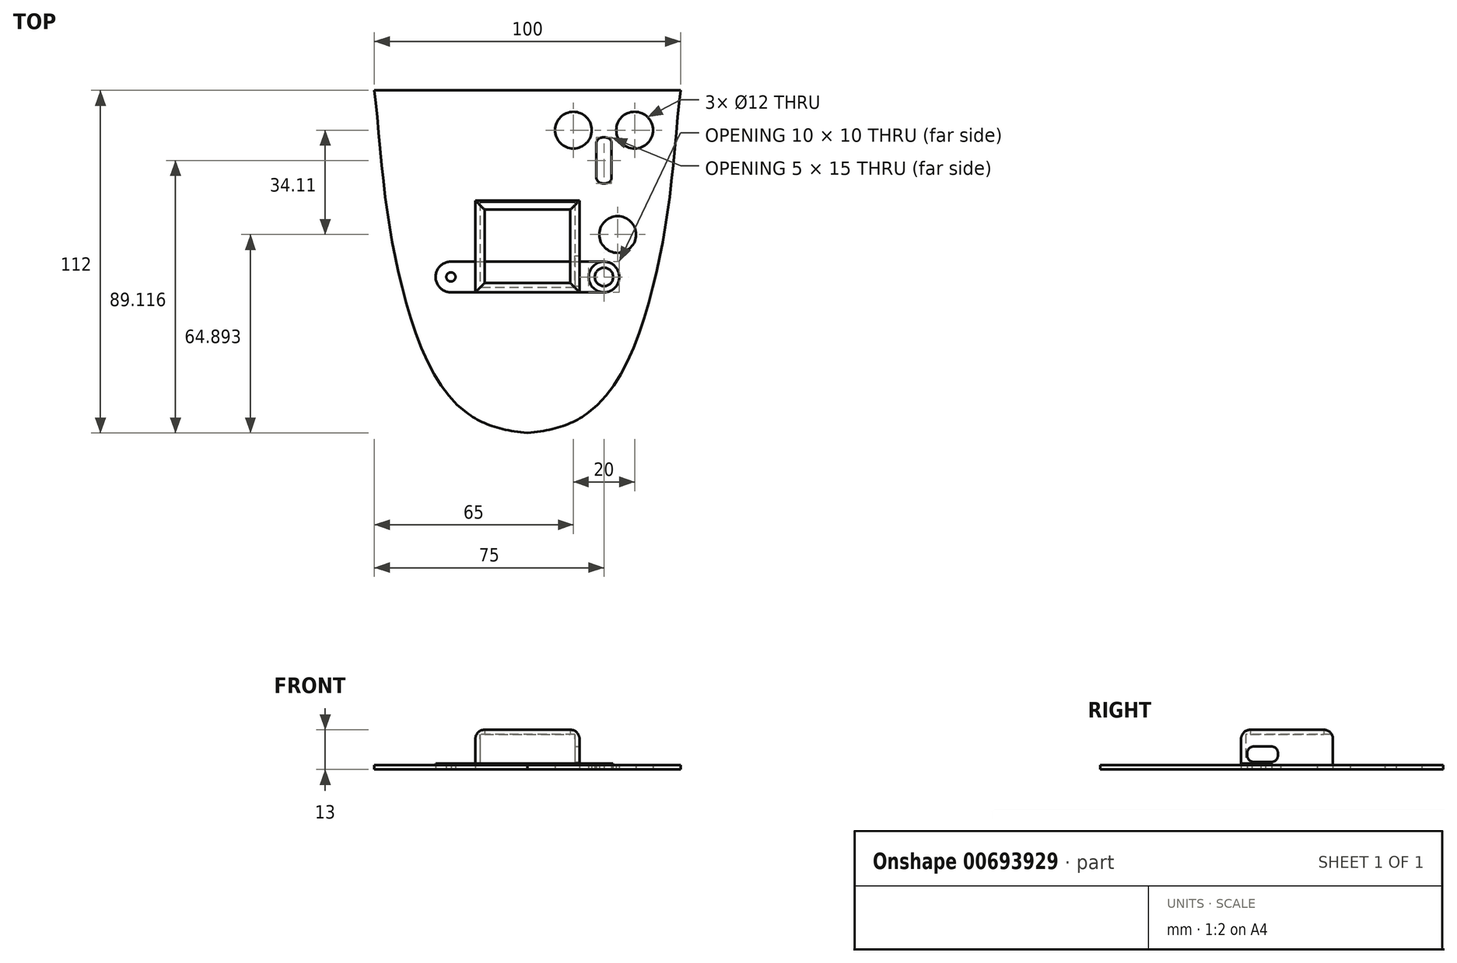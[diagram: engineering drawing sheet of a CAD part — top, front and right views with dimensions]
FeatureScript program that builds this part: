
annotation { "Feature Type Name" : "Feature", "Feature Type Description" : "" }
export const myFeature = defineFeature(function(context is Context, id is Id, definition is map)
    precondition{}
    {
        {
            var Q0;
            Q0=qCreatedBy(makeId("Top.planeOp"),FACE);
            var sketch = newSketch(context, id + "F0", { "sketchPlane" : qUnion([Q0])});
            skLineSegment(sketch, "E0", {"start": v(0, 74.67) * mm, "end": v(50, 74.67) * mm});
            skLineSegment(sketch, "E1", {"start": v(0, 74.67) * mm, "end": v(0, -37.33) * mm});
            skFitSpline(sketch, "E2", {"points": [v(50, 74.67) * mm, v(47, 44.67) * mm, v(42, 14.67) * mm, v(32, -15.33) * mm, v(19, -31.33) * mm, v(0, -37.33) * mm], "startDerivative": vector(-13.36, -107.56) * mm, "endDerivative": vector(-138.13, -13.22) * mm});
            skLineSegment(sketch, "E3.MirrorCS", {"start": v(0, 74.67) * mm, "end": v(-50, 74.67) * mm});
            skFitSpline(sketch, "E4.MirrorCS", {"points": [v(-50, 74.67) * mm, v(-47, 44.67) * mm, v(-42, 14.67) * mm, v(-32, -15.33) * mm, v(-19, -31.33) * mm, v(0, -37.33) * mm], "startDerivative": vector(13.36, -107.56) * mm, "endDerivative": vector(138.13, -13.22) * mm});
            skLineSegment(sketch, "E5.bottom", {"start": v(17, 38.67) * mm, "end": v(-17, 38.67) * mm});
            skLineSegment(sketch, "E5.top", {"start": v(17, 8.67) * mm, "end": v(-17, 8.67) * mm});
            skLineSegment(sketch, "E5.left", {"start": v(17, 38.67) * mm, "end": v(17, 8.67) * mm});
            skLineSegment(sketch, "E5.right", {"start": v(-17, 38.67) * mm, "end": v(-17, 8.67) * mm});
            skPoint(sketch, "E5.middle", {"position": v(0, 23.67) * mm});
            skCircle(sketch, "E6", {"center": v(-25, 13.67) * mm, "radius": 1.5 * mm});
            skCircle(sketch, "E7.MirrorC", {"center": v(25, 13.67) * mm, "radius": 1.5 * mm});
            skCircle(sketch, "E8", {"center": v(-25, 13.67) * mm, "radius": 3 * mm});
            skCircle(sketch, "E9.MirrorC", {"center": v(25, 13.67) * mm, "radius": 3 * mm});
            skLineSegment(sketch, "E10.left", {"start": v(0, 69.67) * mm, "end": v(0, 64.67) * mm});
            skLineSegment(sketch, "E11.bottom", {"start": v(20, 7.67) * mm, "end": v(-20, 7.67) * mm});
            skLineSegment(sketch, "E11.top", {"start": v(20, -58.33) * mm, "end": v(-20, -58.33) * mm});
            skLineSegment(sketch, "E11.left", {"start": v(20, 7.67) * mm, "end": v(20, -58.33) * mm});
            skLineSegment(sketch, "E11.right", {"start": v(-20, 7.67) * mm, "end": v(-20, -58.33) * mm});
            skPoint(sketch, "E11.middle", {"position": v(0, -25.33) * mm});
            skLineSegment(sketch, "E12.bottom", {"start": v(22.5, 59.29) * mm, "end": v(27.5, 59.29) * mm});
            skLineSegment(sketch, "E12.top", {"start": v(22.5, 44.29) * mm, "end": v(27.5, 44.29) * mm});
            skLineSegment(sketch, "E12.left", {"start": v(22.5, 59.29) * mm, "end": v(22.5, 44.29) * mm});
            skLineSegment(sketch, "E12.right", {"start": v(27.5, 59.29) * mm, "end": v(27.5, 44.29) * mm});
            skCircle(sketch, "E13", {"center": v(-25, 13.67) * mm, "radius": 5 * mm});
            skCircle(sketch, "E14.MirrorC", {"center": v(25, 13.67) * mm, "radius": 5 * mm});
            skLineSegment(sketch, "E15", {"start": v(-24.85, 18.67) * mm, "end": v(25, 18.67) * mm});
            skLineSegment(sketch, "E16", {"start": v(-25, 8.67) * mm, "end": v(25, 8.67) * mm});
            skLineSegment(sketch, "E17.bottom", {"start": v(14, 35.67) * mm, "end": v(-14, 35.67) * mm});
            skLineSegment(sketch, "E17.top", {"start": v(14, 11.67) * mm, "end": v(-14, 11.67) * mm});
            skLineSegment(sketch, "E17.left", {"start": v(14, 35.67) * mm, "end": v(14, 11.67) * mm});
            skLineSegment(sketch, "E17.right", {"start": v(-14, 35.67) * mm, "end": v(-14, 11.67) * mm});
            skCircle(sketch, "E18", {"center": v(-35, 61.67) * mm, "radius": 6 * mm});
            skCircle(sketch, "E19", {"center": v(-15, 61.67) * mm, "radius": 6 * mm});
            skCircle(sketch, "E20", {"center": v(-25, 47.67) * mm, "radius": 6 * mm});
            skCircle(sketch, "E21", {"center": v(-29.47, 27.56) * mm, "radius": 6 * mm});
            skCircle(sketch, "E22", {"center": v(-18.64, -7.33) * mm, "radius": 6 * mm});
            skCircle(sketch, "E23", {"center": v(0, -7.33) * mm, "radius": 6 * mm});
            skCircle(sketch, "E24", {"center": v(0, -27.12) * mm, "radius": 6 * mm});
            skCircle(sketch, "E25.MirrorC", {"center": v(35, 61.67) * mm, "radius": 6 * mm});
            skCircle(sketch, "E26.MirrorC", {"center": v(29.47, 27.56) * mm, "radius": 6 * mm});
            skCircle(sketch, "E27.MirrorC", {"center": v(18.64, -7.33) * mm, "radius": 6 * mm});
            skCircle(sketch, "E28.MirrorC", {"center": v(15, 61.67) * mm, "radius": 6 * mm});
            skSolve(sketch);
        }
        {
            var Q0;
            {var subQ6=sQuery(id+"F0.wireOp",EDGE,"E0");Q0=makeQuery(id+"F0.imprint","IMPRINT",FACE,{"disambiguationData":[TD([[makeQuery(id+"F0.imprint","IMPRINT",EDGE,{"derivedFrom":subQ6}),-1.0]])]});}
            var Q1;
            {var subQ1=sQuery(id+"F0.wireOp",EDGE,"E3.MirrorCS");Q1=makeQuery(id+"F0.imprint","IMPRINT",FACE,{"disambiguationData":[TD([[makeQuery(id+"F0.imprint","IMPRINT",EDGE,{"derivedFrom":subQ1}),1.0]])]});}
            var Q2;
            {var subQ5=sQuery(id+"F0.wireOp",EDGE,"E5.right");Q2=makeQuery(id+"F0.imprint","IMPRINT",FACE,{"disambiguationData":[TD([[makeQuery(id+"F0.imprint","IMPRINT",EDGE,{"derivedFrom":subQ5}),1.0]])]});}
            var Q3;
            {var subQ5=sQuery(id+"F0.wireOp",EDGE,"E5.left");Q3=makeQuery(id+"F0.imprint","IMPRINT",FACE,{"disambiguationData":[TD([[makeQuery(id+"F0.imprint","IMPRINT",EDGE,{"derivedFrom":subQ5}),-1.0]])]});}
            var Q4;
            Q4=makeQuery(id+"F0.imprint","IMPRINT",FACE,{"disambiguationData":[TD([[makeQuery(id+"F0.imprint","IMPRINT",EDGE,{"derivedFrom":sQuery(id+"F0.wireOp",EDGE,"E6")}),-1.0]])]});
            var Q5;
            Q5=makeQuery(id+"F0.imprint","IMPRINT",FACE,{"disambiguationData":[TD([[makeQuery(id+"F0.imprint","IMPRINT",EDGE,{"derivedFrom":sQuery(id+"F0.wireOp",EDGE,"E7.MirrorC")}),1.0]])]});
            var Q6;
            {var subQ0=sQuery(id+"F0.wireOp",EDGE,"E16");var subQ1=sQuery(id+"F0.wireOp",EDGE,"E5.right");var subQ2=makeQuery(id+"F0.imprint","INTERSECT",VERTEX,{"derivedFrom":[subQ1,subQ0]});Q6=makeQuery(id+"F0.imprint","IMPRINT",FACE,{"disambiguationData":[TD([[makeQuery(id+"F0.imprint","IMPRINT",EDGE,{"disambiguationData":[TD([[subQ2,1.0]])],"derivedFrom":subQ1}),-1.0]])]});}
            var Q7;
            Q7=makeQuery(id+"F0.imprint","IMPRINT",FACE,{"disambiguationData":[TD([[makeQuery(id+"F0.imprint","IMPRINT",EDGE,{"derivedFrom":sQuery(id+"F0.wireOp",EDGE,"E8")}),-1.0]])]});
            var Q8;
            {var subQ0=sQuery(id+"F0.wireOp",EDGE,"E16");var subQ1=sQuery(id+"F0.wireOp",EDGE,"E5.left");var subQ2=makeQuery(id+"F0.imprint","INTERSECT",VERTEX,{"derivedFrom":[subQ1,subQ0]});Q8=makeQuery(id+"F0.imprint","IMPRINT",FACE,{"disambiguationData":[TD([[makeQuery(id+"F0.imprint","IMPRINT",EDGE,{"disambiguationData":[TD([[subQ2,1.0]])],"derivedFrom":subQ1}),1.0]])]});}
            var Q9;
            Q9=makeQuery(id+"F0.imprint","IMPRINT",FACE,{"disambiguationData":[TD([[makeQuery(id+"F0.imprint","IMPRINT",EDGE,{"derivedFrom":sQuery(id+"F0.wireOp",EDGE,"E9.MirrorC")}),1.0]])]});
            var Q10;
            {var subQ3=sQuery(id+"F0.wireOp",EDGE,"E11.bottom");var subQ5=sQuery(id+"F0.wireOp",EDGE,"E11.right");var subQ7=makeQuery(id+"F0.imprint","INTERSECT",VERTEX,{"derivedFrom":[subQ3,subQ5]});Q10=makeQuery(id+"F0.imprint","IMPRINT",FACE,{"disambiguationData":[TD([[makeQuery(id+"F0.imprint","IMPRINT",EDGE,{"disambiguationData":[TD([[subQ7,1.0]])],"derivedFrom":subQ3}),1.0]])]});}
            var Q11;
            {var subQ3=sQuery(id+"F0.wireOp",EDGE,"E11.bottom");var subQ5=sQuery(id+"F0.wireOp",EDGE,"E11.left");var subQ6=makeQuery(id+"F0.imprint","INTERSECT",VERTEX,{"derivedFrom":[subQ3,subQ5]});Q11=makeQuery(id+"F0.imprint","IMPRINT",FACE,{"disambiguationData":[TD([[makeQuery(id+"F0.imprint","IMPRINT",EDGE,{"disambiguationData":[TD([[subQ6,-1.0]])],"derivedFrom":subQ3}),1.0]])]});}
            var Q12;
            {var subQ0=sQuery(id+"F0.wireOp",EDGE,"E17.bottom");var subQ1=sQuery(id+"F0.wireOp",EDGE,"E1");var subQ2=makeQuery(id+"F0.imprint","INTERSECT",VERTEX,{"derivedFrom":[subQ1,subQ0]});Q12=makeQuery(id+"F0.imprint","IMPRINT",FACE,{"disambiguationData":[TD([[makeQuery(id+"F0.imprint","IMPRINT",EDGE,{"disambiguationData":[TD([[subQ2,-1.0]])],"derivedFrom":subQ1}),-1.0]])]});}
            var Q13;
            {var subQ0=sQuery(id+"F0.wireOp",EDGE,"E17.bottom");var subQ1=sQuery(id+"F0.wireOp",EDGE,"E1");var subQ2=makeQuery(id+"F0.imprint","INTERSECT",VERTEX,{"derivedFrom":[subQ1,subQ0]});Q13=makeQuery(id+"F0.imprint","IMPRINT",FACE,{"disambiguationData":[TD([[makeQuery(id+"F0.imprint","IMPRINT",EDGE,{"disambiguationData":[TD([[subQ2,-1.0]])],"derivedFrom":subQ1}),1.0]])]});}
            var Q14;
            {var subQ0=sQuery(id+"F0.wireOp",EDGE,"E15");var subQ1=sQuery(id+"F0.wireOp",EDGE,"E1");var subQ2=makeQuery(id+"F0.imprint","INTERSECT",VERTEX,{"derivedFrom":[subQ1,subQ0]});Q14=makeQuery(id+"F0.imprint","IMPRINT",FACE,{"disambiguationData":[TD([[makeQuery(id+"F0.imprint","IMPRINT",EDGE,{"disambiguationData":[TD([[subQ2,-1.0]])],"derivedFrom":subQ1}),1.0]])]});}
            var Q15;
            {var subQ0=sQuery(id+"F0.wireOp",EDGE,"E15");var subQ1=sQuery(id+"F0.wireOp",EDGE,"E1");var subQ2=makeQuery(id+"F0.imprint","INTERSECT",VERTEX,{"derivedFrom":[subQ1,subQ0]});Q15=makeQuery(id+"F0.imprint","IMPRINT",FACE,{"disambiguationData":[TD([[makeQuery(id+"F0.imprint","IMPRINT",EDGE,{"disambiguationData":[TD([[subQ2,-1.0]])],"derivedFrom":subQ1}),-1.0]])]});}
            var Q16;
            Q16=makeQuery(id+"F0.imprint","IMPRINT",FACE,{"disambiguationData":[TD([[makeQuery(id+"F0.imprint","IMPRINT",EDGE,{"derivedFrom":sQuery(id+"F0.wireOp",EDGE,"E18")}),1.0]])]});
            var Q17;
            Q17=makeQuery(id+"F0.imprint","IMPRINT",FACE,{"disambiguationData":[TD([[makeQuery(id+"F0.imprint","IMPRINT",EDGE,{"derivedFrom":sQuery(id+"F0.wireOp",EDGE,"E19")}),1.0]])]});
            var Q18;
            Q18=makeQuery(id+"F0.imprint","IMPRINT",FACE,{"disambiguationData":[TD([[makeQuery(id+"F0.imprint","IMPRINT",EDGE,{"derivedFrom":sQuery(id+"F0.wireOp",EDGE,"E20")}),1.0]])]});
            var Q19;
            Q19=makeQuery(id+"F0.imprint","IMPRINT",FACE,{"disambiguationData":[TD([[makeQuery(id+"F0.imprint","IMPRINT",EDGE,{"derivedFrom":sQuery(id+"F0.wireOp",EDGE,"E21")}),1.0]])]});
            var Q20;
            Q20=makeQuery(id+"F0.imprint","IMPRINT",FACE,{"disambiguationData":[TD([[makeQuery(id+"F0.imprint","IMPRINT",EDGE,{"derivedFrom":sQuery(id+"F0.wireOp",EDGE,"E28.MirrorC")}),-1.0]])]});
            var Q21;
            Q21=makeQuery(id+"F0.imprint","IMPRINT",FACE,{"disambiguationData":[TD([[makeQuery(id+"F0.imprint","IMPRINT",EDGE,{"derivedFrom":sQuery(id+"F0.wireOp",EDGE,"E25.MirrorC")}),-1.0]])]});
            var Q22;
            Q22=makeQuery(id+"F0.imprint","IMPRINT",FACE,{"disambiguationData":[TD([[makeQuery(id+"F0.imprint","IMPRINT",EDGE,{"derivedFrom":sQuery(id+"F0.wireOp",EDGE,"E26.MirrorC")}),-1.0]])]});
            var Q23;
            {var subQ0=sQuery(id+"F0.wireOp",EDGE,"E27.MirrorC");var subQ1=sQuery(id+"F0.wireOp",EDGE,"E11.left");var subQ2=makeQuery(id+"F0.imprint","INTERSECT",VERTEX,{"disambiguationData":[OD(0.0)],"derivedFrom":[subQ1,subQ0]});Q23=makeQuery(id+"F0.imprint","IMPRINT",FACE,{"disambiguationData":[TD([[makeQuery(id+"F0.imprint","IMPRINT",EDGE,{"disambiguationData":[TD([[subQ2,-1.0]])],"derivedFrom":subQ1}),1.0]])]});}
            var Q24;
            {var subQ0=sQuery(id+"F0.wireOp",EDGE,"E27.MirrorC");var subQ1=sQuery(id+"F0.wireOp",EDGE,"E11.left");var subQ2=makeQuery(id+"F0.imprint","INTERSECT",VERTEX,{"disambiguationData":[OD(0.0)],"derivedFrom":[subQ1,subQ0]});Q24=makeQuery(id+"F0.imprint","IMPRINT",FACE,{"disambiguationData":[TD([[makeQuery(id+"F0.imprint","IMPRINT",EDGE,{"disambiguationData":[TD([[subQ2,-1.0]])],"derivedFrom":subQ1}),-1.0]])]});}
            var Q25;
            {var subQ0=sQuery(id+"F0.wireOp",EDGE,"E23");var subQ1=sQuery(id+"F0.wireOp",EDGE,"E1");var subQ2=makeQuery(id+"F0.imprint","INTERSECT",VERTEX,{"disambiguationData":[OD(0.0)],"derivedFrom":[subQ1,subQ0]});Q25=makeQuery(id+"F0.imprint","IMPRINT",FACE,{"disambiguationData":[TD([[makeQuery(id+"F0.imprint","IMPRINT",EDGE,{"disambiguationData":[TD([[subQ2,-1.0]])],"derivedFrom":subQ1}),1.0]])]});}
            var Q26;
            {var subQ0=sQuery(id+"F0.wireOp",EDGE,"E23");var subQ1=sQuery(id+"F0.wireOp",EDGE,"E1");var subQ2=makeQuery(id+"F0.imprint","INTERSECT",VERTEX,{"disambiguationData":[OD(0.0)],"derivedFrom":[subQ1,subQ0]});Q26=makeQuery(id+"F0.imprint","IMPRINT",FACE,{"disambiguationData":[TD([[makeQuery(id+"F0.imprint","IMPRINT",EDGE,{"disambiguationData":[TD([[subQ2,-1.0]])],"derivedFrom":subQ1}),-1.0]])]});}
            var Q27;
            {var subQ0=sQuery(id+"F0.wireOp",EDGE,"E22");var subQ1=sQuery(id+"F0.wireOp",EDGE,"E11.right");var subQ2=makeQuery(id+"F0.imprint","INTERSECT",VERTEX,{"disambiguationData":[OD(0.0)],"derivedFrom":[subQ1,subQ0]});Q27=makeQuery(id+"F0.imprint","IMPRINT",FACE,{"disambiguationData":[TD([[makeQuery(id+"F0.imprint","IMPRINT",EDGE,{"disambiguationData":[TD([[subQ2,-1.0]])],"derivedFrom":subQ1}),1.0]])]});}
            var Q28;
            {var subQ0=sQuery(id+"F0.wireOp",EDGE,"E22");var subQ1=sQuery(id+"F0.wireOp",EDGE,"E11.right");var subQ2=makeQuery(id+"F0.imprint","INTERSECT",VERTEX,{"disambiguationData":[OD(0.0)],"derivedFrom":[subQ1,subQ0]});Q28=makeQuery(id+"F0.imprint","IMPRINT",FACE,{"disambiguationData":[TD([[makeQuery(id+"F0.imprint","IMPRINT",EDGE,{"disambiguationData":[TD([[subQ2,-1.0]])],"derivedFrom":subQ1}),-1.0]])]});}
            var Q29;
            {var subQ0=sQuery(id+"F0.wireOp",EDGE,"E24");var subQ1=sQuery(id+"F0.wireOp",EDGE,"E1");var subQ2=makeQuery(id+"F0.imprint","INTERSECT",VERTEX,{"disambiguationData":[OD(0.0)],"derivedFrom":[subQ1,subQ0]});Q29=makeQuery(id+"F0.imprint","IMPRINT",FACE,{"disambiguationData":[TD([[makeQuery(id+"F0.imprint","IMPRINT",EDGE,{"disambiguationData":[TD([[subQ2,-1.0]])],"derivedFrom":subQ1}),-1.0]])]});}
            var Q30;
            {var subQ0=sQuery(id+"F0.wireOp",EDGE,"E24");var subQ1=sQuery(id+"F0.wireOp",EDGE,"E1");var subQ2=makeQuery(id+"F0.imprint","INTERSECT",VERTEX,{"disambiguationData":[OD(0.0)],"derivedFrom":[subQ1,subQ0]});Q30=makeQuery(id+"F0.imprint","IMPRINT",FACE,{"disambiguationData":[TD([[makeQuery(id+"F0.imprint","IMPRINT",EDGE,{"disambiguationData":[TD([[subQ2,-1.0]])],"derivedFrom":subQ1}),1.0]])]});}
            extrude(context, id + "F1", {"entities" : qUnion([Q0, Q1, Q2, Q3, Q4, Q5, Q6, Q7, Q8, Q9, Q10, Q11, Q12, Q13, Q14, Q15, Q16, Q17, Q18, Q19, Q20, Q21, Q22, Q23, Q24, Q25, Q26, Q27, Q28, Q29, Q30]), "depth" : 1.5 * mm, "offsetDistance" : 25 * mm});
        }
        {
            var Q0;
            {var subQ0=sQuery(id+"F0.wireOp",EDGE,"E17.bottom");var subQ1=sQuery(id+"F0.wireOp",EDGE,"E1");var subQ2=makeQuery(id+"F0.imprint","INTERSECT",VERTEX,{"derivedFrom":[subQ1,subQ0]});Q0=makeQuery(id+"F0.imprint","IMPRINT",FACE,{"disambiguationData":[TD([[makeQuery(id+"F0.imprint","IMPRINT",EDGE,{"disambiguationData":[TD([[subQ2,-1.0]])],"derivedFrom":subQ1}),-1.0]])]});}
            var Q1;
            {var subQ0=sQuery(id+"F0.wireOp",EDGE,"E17.bottom");var subQ1=sQuery(id+"F0.wireOp",EDGE,"E1");var subQ2=makeQuery(id+"F0.imprint","INTERSECT",VERTEX,{"derivedFrom":[subQ1,subQ0]});Q1=makeQuery(id+"F0.imprint","IMPRINT",FACE,{"disambiguationData":[TD([[makeQuery(id+"F0.imprint","IMPRINT",EDGE,{"disambiguationData":[TD([[subQ2,-1.0]])],"derivedFrom":subQ1}),1.0]])]});}
            var Q2;
            {var subQ0=sQuery(id+"F0.wireOp",EDGE,"E15");var subQ1=sQuery(id+"F0.wireOp",EDGE,"E1");var subQ2=makeQuery(id+"F0.imprint","INTERSECT",VERTEX,{"derivedFrom":[subQ1,subQ0]});Q2=makeQuery(id+"F0.imprint","IMPRINT",FACE,{"disambiguationData":[TD([[makeQuery(id+"F0.imprint","IMPRINT",EDGE,{"disambiguationData":[TD([[subQ2,-1.0]])],"derivedFrom":subQ1}),1.0]])]});}
            var Q3;
            {var subQ0=sQuery(id+"F0.wireOp",EDGE,"E15");var subQ1=sQuery(id+"F0.wireOp",EDGE,"E1");var subQ2=makeQuery(id+"F0.imprint","INTERSECT",VERTEX,{"derivedFrom":[subQ1,subQ0]});Q3=makeQuery(id+"F0.imprint","IMPRINT",FACE,{"disambiguationData":[TD([[makeQuery(id+"F0.imprint","IMPRINT",EDGE,{"disambiguationData":[TD([[subQ2,-1.0]])],"derivedFrom":subQ1}),-1.0]])]});}
            var Q4;
            {var subQ5=sQuery(id+"F0.wireOp",EDGE,"E5.bottom");var subQ7=sQuery(id+"F0.wireOp",EDGE,"E1");var subQ8=makeQuery(id+"F0.imprint","INTERSECT",VERTEX,{"derivedFrom":[subQ7,subQ5]});Q4=makeQuery(id+"F0.imprint","IMPRINT",FACE,{"disambiguationData":[TD([[makeQuery(id+"F0.imprint","IMPRINT",EDGE,{"disambiguationData":[TD([[subQ8,-1.0]])],"derivedFrom":subQ7}),-1.0]])]});}
            var Q5;
            {var subQ1=sQuery(id+"F0.wireOp",EDGE,"E5.bottom");var subQ7=sQuery(id+"F0.wireOp",EDGE,"E1");var subQ8=makeQuery(id+"F0.imprint","INTERSECT",VERTEX,{"derivedFrom":[subQ7,subQ1]});Q5=makeQuery(id+"F0.imprint","IMPRINT",FACE,{"disambiguationData":[TD([[makeQuery(id+"F0.imprint","IMPRINT",EDGE,{"disambiguationData":[TD([[subQ8,-1.0]])],"derivedFrom":subQ7}),1.0]])]});}
            var Q6;
            {var subQ3=sQuery(id+"F0.wireOp",EDGE,"E1");var subQ9=sQuery(id+"F0.wireOp",EDGE,"E17.top");var subQ11=makeQuery(id+"F0.imprint","INTERSECT",VERTEX,{"derivedFrom":[subQ3,subQ9]});Q6=makeQuery(id+"F0.imprint","IMPRINT",FACE,{"disambiguationData":[TD([[makeQuery(id+"F0.imprint","IMPRINT",EDGE,{"disambiguationData":[TD([[subQ11,-1.0]])],"derivedFrom":subQ3}),1.0]])]});}
            var Q7;
            {var subQ3=sQuery(id+"F0.wireOp",EDGE,"E1");var subQ9=sQuery(id+"F0.wireOp",EDGE,"E17.top");var subQ10=makeQuery(id+"F0.imprint","INTERSECT",VERTEX,{"derivedFrom":[subQ3,subQ9]});Q7=makeQuery(id+"F0.imprint","IMPRINT",FACE,{"disambiguationData":[TD([[makeQuery(id+"F0.imprint","IMPRINT",EDGE,{"disambiguationData":[TD([[subQ10,-1.0]])],"derivedFrom":subQ3}),-1.0]])]});}
            extrude(context, id + "F2", {"entities" : qUnion([Q0, Q1, Q2, Q3, Q4, Q5, Q6, Q7]), "depth" : 13 * mm, "offsetDistance" : 25 * mm});
        }
        {
            var Q0;
            Q0=makeQuery(id+"F2.opExtrude","SWEPT_FACE",FACE,{"disambiguationData":[OSD([sQuery(id+"F0.wireOp",EDGE,"E16")])]});
            var Q1;
            Q1=makeQuery(id+"F2.opExtrude","SWEPT_FACE",FACE,{"disambiguationData":[OSD([sQuery(id+"F0.wireOp",EDGE,"E5.bottom")])]});
            shell(context, id + "F3", {"entities" : qUnion([Q0, Q1]), "thickness" : 1.5 * mm});
        }
        {
            var Q0;
            Q0=makeQuery(id+"F2.opExtrude","CAP_EDGE",EDGE,{"disambiguationData":[OSD([sQuery(id+"F0.wireOp",EDGE,"E5.right")])],"isStart":false});
            var Q1;
            Q1=makeQuery(id+"F2.opExtrude","CAP_EDGE",EDGE,{"disambiguationData":[OSD([sQuery(id+"F0.wireOp",EDGE,"E5.left")])],"isStart":false});
            var Q2;
            Q2=makeQuery(id+"F2.opExtrude","CAP_EDGE",EDGE,{"disambiguationData":[OSD([sQuery(id+"F0.wireOp",EDGE,"E5.top")])],"isStart":false});
            var Q3;
            Q3=makeQuery(id+"F2.opExtrude","CAP_EDGE",EDGE,{"disambiguationData":[OSD([sQuery(id+"F0.wireOp",EDGE,"E5.bottom")])],"isStart":false});
            var Q4;
            Q4=makeQuery(id+"F2.opExtrude","CAP_EDGE",EDGE,{"disambiguationData":[OSD([sQuery(id+"F0.wireOp",EDGE,"E16")])],"isStart":false});
            fillet(context, id + "F4", {"entities" : qUnion([Q0, Q1, Q2, Q3, Q4]), "radius" : 3 * mm, "tangentPropagation" : true, "allowEdgeOverflow" : false});
        }
        {
            var Q0;
            Q0=makeQuery(id+"F1.opExtrude","SWEPT_EDGE",EDGE,{"disambiguationData":[OSD([sQuery(id+"F0.wireOp",EDGE,"E12.bottom"),sQuery(id+"F0.wireOp",EDGE,"E12.left")])]});
            var Q1;
            Q1=makeQuery(id+"F1.opExtrude","SWEPT_EDGE",EDGE,{"disambiguationData":[OSD([sQuery(id+"F0.wireOp",EDGE,"E12.bottom"),sQuery(id+"F0.wireOp",EDGE,"E12.right")])]});
            var Q2;
            Q2=makeQuery(id+"F1.opExtrude","SWEPT_EDGE",EDGE,{"disambiguationData":[OSD([sQuery(id+"F0.wireOp",EDGE,"E12.top"),sQuery(id+"F0.wireOp",EDGE,"E12.right")])]});
            var Q3;
            Q3=makeQuery(id+"F1.opExtrude","SWEPT_EDGE",EDGE,{"disambiguationData":[OSD([sQuery(id+"F0.wireOp",EDGE,"E12.top"),sQuery(id+"F0.wireOp",EDGE,"E12.left")])]});
            fillet(context, id + "F5", {"entities" : qUnion([Q0, Q1, Q2, Q3]), "radius" : 2 * mm, "tangentPropagation" : true, "allowEdgeOverflow" : false});
        }
        {
            var Q0;
            {var subQ0=sQuery(id+"F0.wireOp",EDGE,"E15");var subQ1=sQuery(id+"F0.wireOp",EDGE,"E1");var subQ2=makeQuery(id+"F0.imprint","INTERSECT",VERTEX,{"derivedFrom":[subQ1,subQ0]});Q0=makeQuery(id+"F0.imprint","IMPRINT",FACE,{"disambiguationData":[TD([[makeQuery(id+"F0.imprint","IMPRINT",EDGE,{"disambiguationData":[TD([[subQ2,-1.0]])],"derivedFrom":subQ1}),-1.0]])]});}
            var Q1;
            {var subQ0=sQuery(id+"F0.wireOp",EDGE,"E15");var subQ1=sQuery(id+"F0.wireOp",EDGE,"E1");var subQ2=makeQuery(id+"F0.imprint","INTERSECT",VERTEX,{"derivedFrom":[subQ1,subQ0]});Q1=makeQuery(id+"F0.imprint","IMPRINT",FACE,{"disambiguationData":[TD([[makeQuery(id+"F0.imprint","IMPRINT",EDGE,{"disambiguationData":[TD([[subQ2,-1.0]])],"derivedFrom":subQ1}),1.0]])]});}
            var Q2;
            {var subQ0=sQuery(id+"F0.wireOp",EDGE,"E16");var subQ1=sQuery(id+"F0.wireOp",EDGE,"E5.left");var subQ2=makeQuery(id+"F0.imprint","INTERSECT",VERTEX,{"derivedFrom":[subQ1,subQ0]});Q2=makeQuery(id+"F0.imprint","IMPRINT",FACE,{"disambiguationData":[TD([[makeQuery(id+"F0.imprint","IMPRINT",EDGE,{"disambiguationData":[TD([[subQ2,1.0]])],"derivedFrom":subQ1}),1.0]])]});}
            var Q3;
            Q3=makeQuery(id+"F0.imprint","IMPRINT",FACE,{"disambiguationData":[TD([[makeQuery(id+"F0.imprint","IMPRINT",EDGE,{"derivedFrom":sQuery(id+"F0.wireOp",EDGE,"E9.MirrorC")}),1.0]])]});
            var Q4;
            Q4=makeQuery(id+"F0.imprint","IMPRINT",FACE,{"disambiguationData":[TD([[makeQuery(id+"F0.imprint","IMPRINT",EDGE,{"derivedFrom":sQuery(id+"F0.wireOp",EDGE,"E7.MirrorC")}),1.0]])]});
            var Q5;
            Q5=makeQuery(id+"F0.imprint","IMPRINT",FACE,{"disambiguationData":[TD([[makeQuery(id+"F0.imprint","IMPRINT",EDGE,{"derivedFrom":sQuery(id+"F0.wireOp",EDGE,"E8")}),-1.0]])]});
            var Q6;
            Q6=makeQuery(id+"F0.imprint","IMPRINT",FACE,{"disambiguationData":[TD([[makeQuery(id+"F0.imprint","IMPRINT",EDGE,{"derivedFrom":sQuery(id+"F0.wireOp",EDGE,"E6")}),-1.0]])]});
            var Q7;
            {var subQ0=sQuery(id+"F0.wireOp",EDGE,"E16");var subQ1=sQuery(id+"F0.wireOp",EDGE,"E5.right");var subQ2=makeQuery(id+"F0.imprint","INTERSECT",VERTEX,{"derivedFrom":[subQ1,subQ0]});Q7=makeQuery(id+"F0.imprint","IMPRINT",FACE,{"disambiguationData":[TD([[makeQuery(id+"F0.imprint","IMPRINT",EDGE,{"disambiguationData":[TD([[subQ2,1.0]])],"derivedFrom":subQ1}),-1.0]])]});}
            var Q8;
            {var subQ3=sQuery(id+"F0.wireOp",EDGE,"E1");var subQ9=sQuery(id+"F0.wireOp",EDGE,"E17.top");var subQ10=makeQuery(id+"F0.imprint","INTERSECT",VERTEX,{"derivedFrom":[subQ3,subQ9]});Q8=makeQuery(id+"F0.imprint","IMPRINT",FACE,{"disambiguationData":[TD([[makeQuery(id+"F0.imprint","IMPRINT",EDGE,{"disambiguationData":[TD([[subQ10,-1.0]])],"derivedFrom":subQ3}),-1.0]])]});}
            var Q9;
            {var subQ3=sQuery(id+"F0.wireOp",EDGE,"E1");var subQ9=sQuery(id+"F0.wireOp",EDGE,"E17.top");var subQ11=makeQuery(id+"F0.imprint","INTERSECT",VERTEX,{"derivedFrom":[subQ3,subQ9]});Q9=makeQuery(id+"F0.imprint","IMPRINT",FACE,{"disambiguationData":[TD([[makeQuery(id+"F0.imprint","IMPRINT",EDGE,{"disambiguationData":[TD([[subQ11,-1.0]])],"derivedFrom":subQ3}),1.0]])]});}
            extrude(context, id + "F6", {"entities" : qUnion([Q0, Q1, Q2, Q3, Q4, Q5, Q6, Q7, Q8, Q9]), "depth" : 2 * mm, "offsetDistance" : 25 * mm});
        }
        {
            var Q0;
            {var subQ0=sQuery(id+"F0.wireOp",EDGE,"E17.bottom");var subQ1=sQuery(id+"F0.wireOp",EDGE,"E1");var subQ2=makeQuery(id+"F0.imprint","INTERSECT",VERTEX,{"derivedFrom":[subQ1,subQ0]});Q0=makeQuery(id+"F0.imprint","IMPRINT",FACE,{"disambiguationData":[TD([[makeQuery(id+"F0.imprint","IMPRINT",EDGE,{"disambiguationData":[TD([[subQ2,-1.0]])],"derivedFrom":subQ1}),-1.0]])]});}
            var Q1;
            {var subQ0=sQuery(id+"F0.wireOp",EDGE,"E17.bottom");var subQ1=sQuery(id+"F0.wireOp",EDGE,"E1");var subQ2=makeQuery(id+"F0.imprint","INTERSECT",VERTEX,{"derivedFrom":[subQ1,subQ0]});Q1=makeQuery(id+"F0.imprint","IMPRINT",FACE,{"disambiguationData":[TD([[makeQuery(id+"F0.imprint","IMPRINT",EDGE,{"disambiguationData":[TD([[subQ2,-1.0]])],"derivedFrom":subQ1}),1.0]])]});}
            var Q2;
            {var subQ0=sQuery(id+"F0.wireOp",EDGE,"E15");var subQ1=sQuery(id+"F0.wireOp",EDGE,"E1");var subQ2=makeQuery(id+"F0.imprint","INTERSECT",VERTEX,{"derivedFrom":[subQ1,subQ0]});Q2=makeQuery(id+"F0.imprint","IMPRINT",FACE,{"disambiguationData":[TD([[makeQuery(id+"F0.imprint","IMPRINT",EDGE,{"disambiguationData":[TD([[subQ2,-1.0]])],"derivedFrom":subQ1}),1.0]])]});}
            var Q3;
            {var subQ0=sQuery(id+"F0.wireOp",EDGE,"E15");var subQ1=sQuery(id+"F0.wireOp",EDGE,"E1");var subQ2=makeQuery(id+"F0.imprint","INTERSECT",VERTEX,{"derivedFrom":[subQ1,subQ0]});Q3=makeQuery(id+"F0.imprint","IMPRINT",FACE,{"disambiguationData":[TD([[makeQuery(id+"F0.imprint","IMPRINT",EDGE,{"disambiguationData":[TD([[subQ2,-1.0]])],"derivedFrom":subQ1}),-1.0]])]});}
            extrude(context, id + "F7", {"entities" : qUnion([Q0, Q1, Q2, Q3]), "operationType" : NewBodyOperationType.REMOVE, "depth" : 25 * mm, "offsetDistance" : 25 * mm, "hasSecondDirection" : true, "secondDirectionOppositeDirection" : false, "secondDirectionDepth" : 3 * mm});
        }
        {
            var Q0;
            Q0=makeQuery(id+"F2.opExtrude","SWEPT_FACE",FACE,{"disambiguationData":[OSD([sQuery(id+"F0.wireOp",EDGE,"E5.left")])]});
            var sketch = newSketch(context, id + "F8", { "sketchPlane" : qUnion([Q0])});
            skLineSegment(sketch, "E29.bottom", {"start": v(10.67, 7.5) * mm, "end": v(20.67, 7.5) * mm});
            skLineSegment(sketch, "E29.top", {"start": v(10.67, 2.5) * mm, "end": v(20.67, 2.5) * mm});
            skLineSegment(sketch, "E29.left", {"start": v(10.67, 7.5) * mm, "end": v(10.67, 2.5) * mm});
            skLineSegment(sketch, "E29.right", {"start": v(20.67, 7.5) * mm, "end": v(20.67, 2.5) * mm});
            skSolve(sketch);
        }
        {
            var Q0;
            Q0=makeQuery(id+"F8.imprint","IMPRINT",FACE,{"disambiguationData":[TD([[makeQuery(id+"F8.imprint","IMPRINT",EDGE,{"derivedFrom":sQuery(id+"F8.wireOp",EDGE,"E29.bottom")}),-1.0]])]});
            extrude(context, id + "F9", {"entities" : qUnion([Q0]), "operationType" : NewBodyOperationType.REMOVE, "oppositeDirection" : true, "depth" : 5 * mm, "offsetDistance" : 25 * mm});
        }
        {
            var Q0;
            Q0=makeQuery(id+"F9.boolean.opBoolean","COPY",EDGE,{"derivedFrom":makeQuery(id+"F9.opExtrude","SWEPT_EDGE",EDGE,{"disambiguationData":[OSD([sQuery(id+"F8.wireOp",EDGE,"E29.top"),sQuery(id+"F8.wireOp",EDGE,"E29.right")])]})});
            var Q1;
            Q1=makeQuery(id+"F9.boolean.opBoolean","COPY",EDGE,{"derivedFrom":makeQuery(id+"F9.opExtrude","SWEPT_EDGE",EDGE,{"disambiguationData":[OSD([sQuery(id+"F8.wireOp",EDGE,"E29.bottom"),sQuery(id+"F8.wireOp",EDGE,"E29.right")])]})});
            var Q2;
            Q2=makeQuery(id+"F9.boolean.opBoolean","COPY",EDGE,{"derivedFrom":makeQuery(id+"F9.opExtrude","SWEPT_EDGE",EDGE,{"disambiguationData":[OSD([sQuery(id+"F8.wireOp",EDGE,"E29.bottom"),sQuery(id+"F8.wireOp",EDGE,"E29.left")])]})});
            var Q3;
            Q3=makeQuery(id+"F9.boolean.opBoolean","COPY",EDGE,{"derivedFrom":makeQuery(id+"F9.opExtrude","SWEPT_EDGE",EDGE,{"disambiguationData":[OSD([sQuery(id+"F8.wireOp",EDGE,"E29.top"),sQuery(id+"F8.wireOp",EDGE,"E29.left")])]})});
            fillet(context, id + "F10", {"entities" : qUnion([Q0, Q1, Q2, Q3]), "radius" : 2 * mm, "tangentPropagation" : true, "allowEdgeOverflow" : false});
        }
    });
